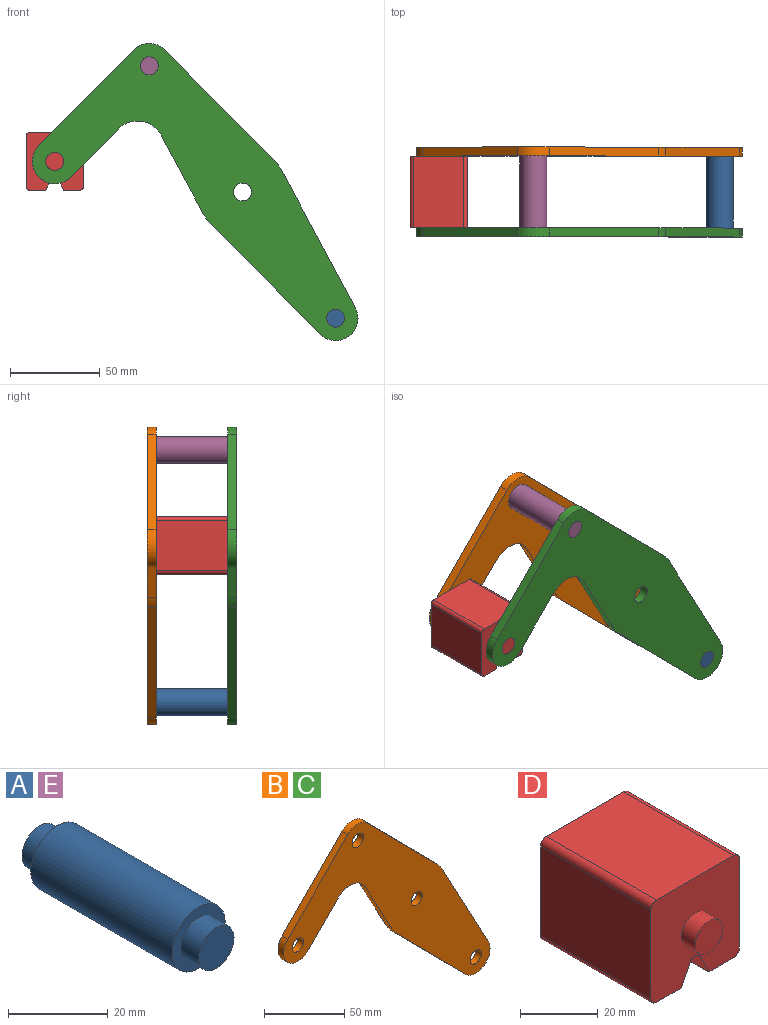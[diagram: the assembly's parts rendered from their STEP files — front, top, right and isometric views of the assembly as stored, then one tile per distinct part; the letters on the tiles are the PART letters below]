
ASSEMBLY  parts=5 mates=3
PART A: 7 faces, bbox 15x50x15 mm
  f0: cylinder r=7.5mm len=40mm, axis (0,-1,0), area 1885mm2, adj f2,f5
  f1: cylinder r=5mm len=10mm, axis (0,1,0), area 157.1mm2, adj f2,f3
  f2: plane 15x15mm, normal (0,-1,0), area 98.2mm2, adj f0,f1
  f3: plane 10x10mm, normal (0,-1,0), area 78.5mm2, adj f1
  f4: cylinder r=5mm len=10mm, axis (0,-1,0), area 157.1mm2, adj f5,f6
  f5: plane 15x15mm, normal (0,1,0), area 98.2mm2, adj f0,f4
  f6: plane 10x10mm, normal (0,1,0), area 78.5mm2, adj f4
PART B: 18 faces, bbox 181.7x5x165.8 mm
  f0: plane 43.49x23.35mm, normal (-0.88,0,-0.47), area 246.8mm2, adj f1,f14,f16,f17
  f1: cylinder r=25mm len=5.75mm, axis (0,1,0), area 35.8mm2, adj f0,f2,f16,f17
  f2: plane 61.6x60.87mm, normal (-0.71,0,-0.7), area 433mm2, adj f1,f3,f16,f17
  f3: cylinder r=12.5mm len=21.39mm, axis (0,1,0), area 178.4mm2, adj f2,f4,f16,f17
  f4: plane 76.3x40.96mm, normal (0.88,0,0.47), area 433mm2, adj f3,f5,f16,f17
  f5: cylinder r=25mm len=5.75mm, axis (0,1,0), area 35.8mm2, adj f4,f6,f16,f17
  f6: plane 61.6x60.87mm, normal (0.71,0,0.7), area 433mm2, adj f5,f7,f16,f17
  f7: cylinder r=12.5mm len=17.78mm, axis (0,1,0), area 98.9mm2, adj f6,f8,f16,f17
  f8: plane 53.35x52.71mm, normal (-0.71,0,0.7), area 375mm2, adj f7,f9,f16,f17
  f9: cylinder r=12.5mm len=21.39mm, axis (0,1,0), area 196.3mm2, adj f8,f10,f16,f17
  f10: plane 26.86x26.54mm, normal (0.71,0,-0.7), area 188.8mm2, adj f9,f14,f16,f17
  f11: cylinder r=5mm len=10mm, axis (0,1,0), area 157.1mm2, adj f16,f17
  f12: cylinder r=5mm len=10mm, axis (0,1,0), area 157.1mm2, adj f16,f17
  f13: cylinder r=5mm len=10mm, axis (0,1,0), area 157.1mm2, adj f16,f17
  f14: cylinder r=15mm len=23.89mm, axis (0,1,0), area 140.2mm2, adj f0,f10,f16,f17
  f15: cylinder r=5mm len=10mm, axis (0,1,0), area 157.1mm2, adj f16,f17
  f16: plane 181.66x165.78mm, normal (0,-1,0), area 8710.1mm2, adj f0,f1,f2,f3,f4,f5,f6,f7
  f17: plane 181.66x165.78mm, normal (0,1,0), area 8710.1mm2, adj f0,f1,f2,f3,f4,f5,f6,f7
PART C: same geometry as B
PART D: 18 faces, bbox 32.1x50x32.1 mm
  f0: plane 40x28.08mm, normal (1,0,0), area 1123.1mm2, adj f4,f10,f13,f14
  f1: plane 40x9.04mm, normal (0,0,-1), area 361.6mm2, adj f2,f4,f10,f14
  f2: plane 40x6.42mm, normal (-0.89,0,-0.45), area 287.2mm2, adj f1,f4,f10,f15
  f3: plane 40x6.42mm, normal (0.89,0,-0.45), area 287.2mm2, adj f4,f5,f10,f15
  f4: plane 32.08x32.08mm, normal (0,-1,0), area 900.6mm2, adj f0,f1,f2,f3,f5,f6,f7,f9
  f5: plane 40x9.04mm, normal (0,0,-1), area 361.6mm2, adj f3,f4,f10,f16
  f6: plane 40x28.08mm, normal (0,0,1), area 1123.1mm2, adj f4,f10,f13,f17
  f7: plane 40x28.08mm, normal (-1,0,0), area 1123.1mm2, adj f4,f10,f16,f17
  f8: plane 10x10mm, normal (0,-1,0), area 78.5mm2, adj f9
  f9: cylinder r=5mm len=10mm, axis (0,1,0), area 157.1mm2, adj f4,f8
  f10: plane 32.08x32.08mm, normal (0,1,0), area 900.6mm2, adj f0,f1,f2,f3,f5,f6,f7,f12
  f11: plane 10x10mm, normal (0,1,0), area 78.5mm2, adj f12
  f12: cylinder r=5mm len=10mm, axis (0,-1,0), area 157.1mm2, adj f10,f11
  f13: cylinder r=2mm len=40mm, axis (0,1,0), area 125.7mm2, adj f0,f4,f6,f10
  f14: cylinder r=2mm len=40mm, axis (0,-1,0), area 125.7mm2, adj f0,f1,f4,f10
  f15: cylinder r=2mm len=40mm, axis (0,1,0), area 177.1mm2, adj f2,f3,f4,f10
  f16: cylinder r=2mm len=40mm, axis (0,1,0), area 125.7mm2, adj f4,f5,f7,f10
  f17: cylinder r=2mm len=40mm, axis (0,-1,0), area 125.7mm2, adj f4,f6,f7,f10
PART E: same geometry as A
PLACE A t=(103.95,-20,-140.78)mm
PLACE B t=(0,25,0)mm
PLACE C t=(0,-20,0)mm fixed
PLACE D t=(0,-20,0)mm
PLACE E t=(0,-20,0)mm
MATE fastened E.f0 <-> B.f7  axis (0,1,0) through (-51.98,20,70.39)mm
MATE revolute D.f9 <-> C.f9  axis (0,1,0) through (-104.69,-20,17.04)mm
MATE fastened C.f3 <-> A.f0  axis (0,1,0) through (51.98,-20,-70.39)mm
